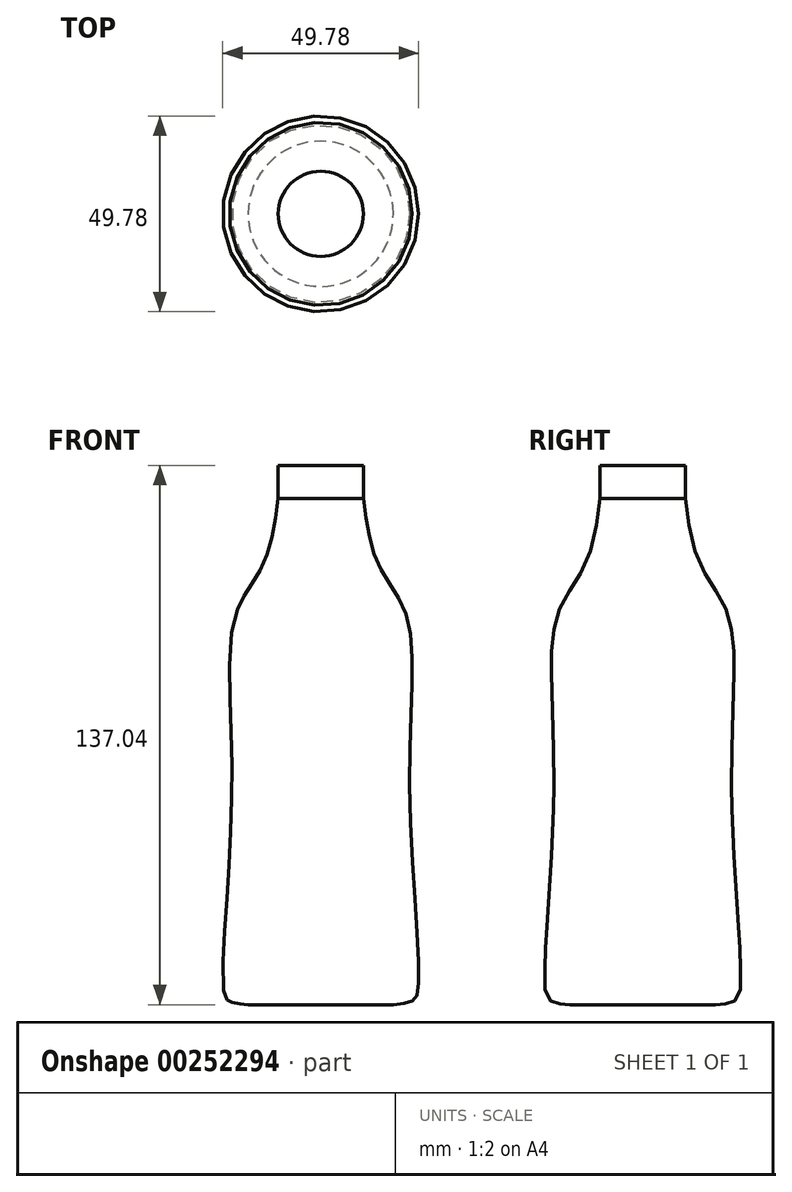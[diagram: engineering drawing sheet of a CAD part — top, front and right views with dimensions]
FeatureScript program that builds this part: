
annotation { "Feature Type Name" : "Feature", "Feature Type Description" : "" }
export const myFeature = defineFeature(function(context is Context, id is Id, definition is map)
    precondition{}
    {
        {
            var Q0;
            Q0=qCreatedBy(makeId("Front.planeOp"),FACE);
            var sketch = newSketch(context, id + "F0", { "sketchPlane" : qUnion([Q0])});
            skLineSegment(sketch, "E0", {"start": v(0, 84.37) * mm, "end": v(0, -83.52) * mm, "construction": true});
            skLineSegment(sketch, "E1", {"start": v(-18.47, -75.88) * mm, "end": v(0, -75.88) * mm});
            skLineSegment(sketch, "E2", {"start": v(-10.82, 52.66) * mm, "end": v(0, 52.66) * mm});
            skLineSegment(sketch, "E3", {"start": v(0, 52.66) * mm, "end": v(0, 61.16) * mm});
            skLineSegment(sketch, "E4", {"start": v(0, 61.16) * mm, "end": v(-10.82, 61.16) * mm});
            skLineSegment(sketch, "E5", {"start": v(-10.82, 61.16) * mm, "end": v(-10.82, 52.66) * mm});
            skLineSegment(sketch, "E6", {"start": v(0, 52.66) * mm, "end": v(0, -75.88) * mm});
            skFitSpline(sketch, "E7", {"points": [v(-10.82, 52.66) * mm, v(-14.66, 35.9) * mm, v(-21.8, 22.74) * mm, v(-22.55, -18.23) * mm, v(-24.8, -71.6) * mm, v(-23.3, -74.98) * mm, v(-18.47, -75.88) * mm], "startDerivative": vector(-14.76, -112.3) * mm, "endDerivative": vector(65.26, -5.4) * mm});
            skSolve(sketch);
        }
        {
            var Q0;
            Q0=makeQuery(id+"F0.imprint","IMPRINT",FACE,{"disambiguationData":[TD([[makeQuery(id+"F0.imprint","IMPRINT",EDGE,{"derivedFrom":sQuery(id+"F0.wireOp",EDGE,"E2")}),1.0]])]});
            var Q1;
            Q1=makeQuery(id+"F0.imprint","IMPRINT",FACE,{"disambiguationData":[TD([[makeQuery(id+"F0.imprint","IMPRINT",EDGE,{"derivedFrom":sQuery(id+"F0.wireOp",EDGE,"E1")}),1.0]])]});
            var Q2;
            Q2=sQuery(id+"F0.wireOp",EDGE,"E0");
            revolve(context, id + "F1", {"entities" : qUnion([Q0, Q1]), "axis" : qUnion([Q2]), "revolveType" : RevolveType.FULL});
        }
    });
